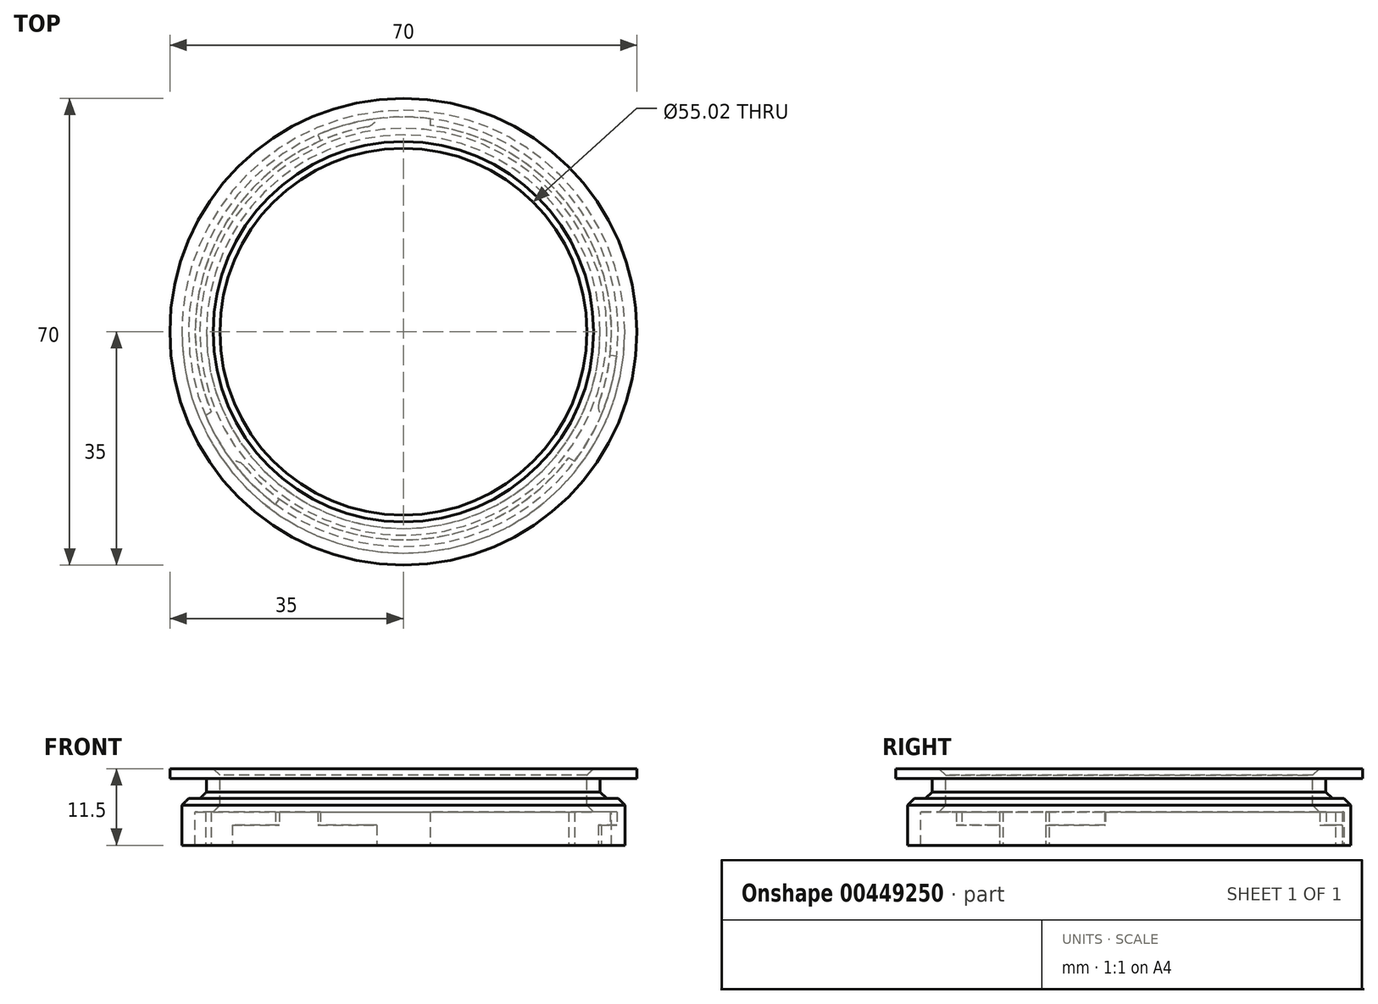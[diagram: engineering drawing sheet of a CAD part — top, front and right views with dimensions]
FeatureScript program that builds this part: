
annotation { "Feature Type Name" : "Feature", "Feature Type Description" : "" }
export const myFeature = defineFeature(function(context is Context, id is Id, definition is map)
    precondition{}
    {
        {
            var Q0;
            Q0=qCreatedBy(makeId("Front.planeOp"),FACE);
            var sketch = newSketch(context, id + "F0", { "sketchPlane" : qUnion([Q0])});
            skLineSegment(sketch, "E0.bottom", {"start": v(33.2, 3.5) * mm, "end": v(-33.2, 3.5) * mm});
            skLineSegment(sketch, "E0.top", {"start": v(33.2, -3.5) * mm, "end": v(-33.2, -3.5) * mm});
            skLineSegment(sketch, "E0.left", {"start": v(33.2, 3.5) * mm, "end": v(33.2, -3.5) * mm});
            skLineSegment(sketch, "E0.right", {"start": v(-33.2, 3.5) * mm, "end": v(-33.2, -3.5) * mm});
            skPoint(sketch, "E0.middle", {"position": v(0, 0) * mm});
            skLineSegment(sketch, "E1.bottom", {"start": v(29.5, 6.5) * mm, "end": v(-29.5, 6.5) * mm});
            skLineSegment(sketch, "E1.left", {"start": v(29.5, 6.5) * mm, "end": v(29.5, -3.5) * mm});
            skLineSegment(sketch, "E1.right", {"start": v(-29.5, 6.5) * mm, "end": v(-29.5, -3.5) * mm});
            skLineSegment(sketch, "E2.bottom", {"start": v(35, 9.5) * mm, "end": v(-35, 9.5) * mm});
            skLineSegment(sketch, "E2.top", {"start": v(35, 6.5) * mm, "end": v(-35, 6.5) * mm});
            skLineSegment(sketch, "E2.left", {"start": v(35, 9.5) * mm, "end": v(35, 6.5) * mm});
            skLineSegment(sketch, "E2.right", {"start": v(-35, 9.5) * mm, "end": v(-35, 6.5) * mm});
            skPoint(sketch, "E2.middle", {"position": v(0, 8) * mm});
            skPoint(sketch, "E2.middle.positionSnap0", {"position": v(0, 6.5) * mm});
            skPoint(sketch, "E2.centerSnap0", {"position": v(0, 6.5) * mm});
            skPoint(sketch, "E3.orphan", {"position": v(-29.5, -6.5) * mm});
            skPoint(sketch, "E1.top.start.orphan", {"position": v(29.5, -6.5) * mm});
            skPoint(sketch, "E4.orphan", {"position": v(0, -6.5) * mm});
            skLineSegment(sketch, "E5", {"start": v(31.2, -3.5) * mm, "end": v(31.2, 1.5) * mm});
            skLineSegment(sketch, "E6", {"start": v(31.2, 1.5) * mm, "end": v(27.5, 1.5) * mm});
            skLineSegment(sketch, "E7", {"start": v(27.5, 1.5) * mm, "end": v(27.5, 9.5) * mm});
            skLineSegment(sketch, "E8", {"start": v(0, 12.55) * mm, "end": v(0, -12.38) * mm});
            skLineSegment(sketch, "E9", {"start": v(-35, 8) * mm, "end": v(35, 8) * mm});
            skSolve(sketch);
        }
        {
            var Q0;
            {var subQ5=sQuery(id+"F0.wireOp",EDGE,"E0.left");Q0=makeQuery(id+"F0.imprint","IMPRINT",FACE,{"disambiguationData":[TD([[makeQuery(id+"F0.imprint","IMPRINT",EDGE,{"derivedFrom":subQ5}),-1.0]])]});}
            var Q1;
            {var subQ0=sQuery(id+"F0.wireOp",EDGE,"E1.left");var subQ1=sQuery(id+"F0.wireOp",EDGE,"E0.bottom");var subQ2=makeQuery(id+"F0.imprint","INTERSECT",VERTEX,{"derivedFrom":[subQ1,subQ0]});Q1=makeQuery(id+"F0.imprint","IMPRINT",FACE,{"disambiguationData":[TD([[makeQuery(id+"F0.imprint","IMPRINT",EDGE,{"disambiguationData":[TD([[subQ2,-1.0]])],"derivedFrom":subQ1}),1.0]])]});}
            var Q2;
            {var subQ0=sQuery(id+"F0.wireOp",EDGE,"E1.left");var subQ1=sQuery(id+"F0.wireOp",EDGE,"E0.bottom");var subQ2=makeQuery(id+"F0.imprint","INTERSECT",VERTEX,{"derivedFrom":[subQ1,subQ0]});Q2=makeQuery(id+"F0.imprint","IMPRINT",FACE,{"disambiguationData":[TD([[makeQuery(id+"F0.imprint","IMPRINT",EDGE,{"disambiguationData":[TD([[subQ2,-1.0]])],"derivedFrom":subQ1}),-1.0]])]});}
            var Q3;
            {var subQ1=sQuery(id+"F0.wireOp",EDGE,"E2.top");var subQ8=makeQuery(id+"F0.imprint","INTERSECT",VERTEX,{"derivedFrom":[sQuery(id+"F0.wireOp",EDGE,"E1.left"),subQ1]});Q3=makeQuery(id+"F0.imprint","IMPRINT",FACE,{"disambiguationData":[TD([[makeQuery(id+"F0.imprint","IMPRINT",EDGE,{"disambiguationData":[TD([[subQ8,1.0]])],"derivedFrom":subQ1}),-1.0]])]});}
            var Q4;
            Q4=sQuery(id+"F0.wireOp",EDGE,"E8");
            revolve(context, id + "F1", {"entities" : qUnion([Q0, Q1, Q2, Q3]), "axis" : qUnion([Q4]), "revolveType" : RevolveType.FULL});
        }
        {
            var Q0;
            Q0=makeQuery(id+"F1.opRevolve","SWEPT_EDGE",EDGE,{"disambiguationData":[OSD([sQuery(id+"F0.wireOp",EDGE,"E0.bottom"),sQuery(id+"F0.wireOp",EDGE,"E0.left")])]});
            var Q1;
            Q1=makeQuery(id+"F1.opRevolve","SWEPT_EDGE",EDGE,{"disambiguationData":[OSD([sQuery(id+"F0.wireOp",EDGE,"E6"),sQuery(id+"F0.wireOp",EDGE,"E7")])]});
            var Q2;
            Q2=makeQuery(id+"F1.opRevolve","SWEPT_EDGE",EDGE,{"disambiguationData":[OSD([sQuery(id+"F0.wireOp",EDGE,"E2.bottom"),sQuery(id+"F0.wireOp",EDGE,"E7")])]});
            var Q3;
            Q3=makeQuery(id+"F1.opRevolve","SWEPT_EDGE",EDGE,{"disambiguationData":[OSD([sQuery(id+"F0.wireOp",EDGE,"E0.bottom"),sQuery(id+"F0.wireOp",EDGE,"E1.left")])]});
            chamfer(context, id + "F2", {"entities" : qUnion([Q0, Q1, Q2, Q3]), "width" : 1 * mm, "tangentPropagation" : true});
        }
        {
            var Q0;
            Q0=makeQuery(id+"F1.opRevolve","SWEPT_FACE",FACE,{"disambiguationData":[OSD([sQuery(id+"F0.wireOp",EDGE,"E0.top")])]});
            var sketch = newSketch(context, id + "F3", { "sketchPlane" : qUnion([Q0])});
            skCircle(sketch, "E10", {"center": v(0, 0) * mm, "radius": 33.2 * mm});
            skCircle(sketch, "E11.0", {"center": v(0, 0) * mm, "radius": 32.2 * mm});
            skLineSegment(sketch, "E12", {"start": v(4, -31.95) * mm, "end": v(4, -30.94) * mm});
            skLineSegment(sketch, "E13.MirrorCS", {"start": v(-4, -31.95) * mm, "end": v(-4, -30.94) * mm});
            skLineSegment(sketch, "E14", {"start": v(0, 0) * mm, "end": v(-12.83, -29.53) * mm});
            skArc(sketch, "E15", {"start": v(4, -30.94) * mm, "mid": v(0, 31.2) * mm, "end": v(-4, -30.94) * mm});
            skLineSegment(sketch, "E16.1.0", {"start": v(25.67, 19.44) * mm, "end": v(24.8, 18.94) * mm});
            skLineSegment(sketch, "E16.1.1", {"start": v(29.67, 12.51) * mm, "end": v(28.8, 12) * mm});
            skLineSegment(sketch, "E16.1.2", {"start": v(0, 0) * mm, "end": v(32, 3.66) * mm});
            skLineSegment(sketch, "E16.2.0", {"start": v(-29.67, 12.51) * mm, "end": v(-28.8, 12) * mm});
            skLineSegment(sketch, "E16.2.1", {"start": v(-25.67, 19.44) * mm, "end": v(-24.8, 18.94) * mm});
            skLineSegment(sketch, "E16.2.2", {"start": v(0, 0) * mm, "end": v(-19.16, 25.88) * mm});
            skSolve(sketch);
        }
        {
            var Q0;
            {var subQ0=sQuery(id+"F3.wireOp",EDGE,"E12");Q0=makeQuery(id+"F3.imprint","IMPRINT",FACE,{"disambiguationData":[TD([[makeQuery(id+"F3.imprint","IMPRINT",EDGE,{"derivedFrom":subQ0}),1.0]])]});}
            var Q1;
            {var subQ0=sQuery(id+"F3.wireOp",EDGE,"E13.MirrorCS");Q1=makeQuery(id+"F3.imprint","IMPRINT",FACE,{"disambiguationData":[TD([[makeQuery(id+"F3.imprint","IMPRINT",EDGE,{"derivedFrom":subQ0}),1.0]])]});}
            var Q2;
            {var subQ0=sQuery(id+"F3.wireOp",EDGE,"E16.2.0");Q2=makeQuery(id+"F3.imprint","IMPRINT",FACE,{"disambiguationData":[TD([[makeQuery(id+"F3.imprint","IMPRINT",EDGE,{"derivedFrom":subQ0}),1.0]])]});}
            var Q3;
            {var subQ0=sQuery(id+"F3.wireOp",EDGE,"E16.2.1");Q3=makeQuery(id+"F3.imprint","IMPRINT",FACE,{"disambiguationData":[TD([[makeQuery(id+"F3.imprint","IMPRINT",EDGE,{"derivedFrom":subQ0}),1.0]])]});}
            var Q4;
            {var subQ0=sQuery(id+"F3.wireOp",EDGE,"E16.1.1");Q4=makeQuery(id+"F3.imprint","IMPRINT",FACE,{"disambiguationData":[TD([[makeQuery(id+"F3.imprint","IMPRINT",EDGE,{"derivedFrom":subQ0}),1.0]])]});}
            var Q5;
            {var subQ0=sQuery(id+"F3.wireOp",EDGE,"E16.1.0");Q5=makeQuery(id+"F3.imprint","IMPRINT",FACE,{"disambiguationData":[TD([[makeQuery(id+"F3.imprint","IMPRINT",EDGE,{"derivedFrom":subQ0}),1.0]])]});}
            var Q6;
            Q6=makeQuery(id+"F1.opRevolve","SWEPT_FACE",FACE,{"disambiguationData":[OSD([sQuery(id+"F0.wireOp",EDGE,"E6")])]});
            extrude(context, id + "F4", {"entities" : qUnion([Q0, Q1, Q2, Q3, Q4, Q5]), "operationType" : NewBodyOperationType.REMOVE, "endBound" : BoundingType.UP_TO_SURFACE, "oppositeDirection" : true, "endBoundEntityFace" : qUnion([Q6]), "depth" : 25 * mm});
        }
        {
            var Q0;
            {var subQ0=sQuery(id+"F3.wireOp",EDGE,"E13.MirrorCS");Q0=makeQuery(id+"F3.imprint","IMPRINT",FACE,{"disambiguationData":[TD([[makeQuery(id+"F3.imprint","IMPRINT",EDGE,{"derivedFrom":subQ0}),1.0]])]});}
            var Q1;
            {var subQ0=sQuery(id+"F3.wireOp",EDGE,"E16.2.1");Q1=makeQuery(id+"F3.imprint","IMPRINT",FACE,{"disambiguationData":[TD([[makeQuery(id+"F3.imprint","IMPRINT",EDGE,{"derivedFrom":subQ0}),1.0]])]});}
            var Q2;
            {var subQ0=sQuery(id+"F3.wireOp",EDGE,"E16.1.1");Q2=makeQuery(id+"F3.imprint","IMPRINT",FACE,{"disambiguationData":[TD([[makeQuery(id+"F3.imprint","IMPRINT",EDGE,{"derivedFrom":subQ0}),1.0]])]});}
            extrude(context, id + "F5", {"entities" : qUnion([Q0, Q1, Q2]), "operationType" : NewBodyOperationType.ADD, "oppositeDirection" : true, "depth" : 3 * mm});
        }
        {
            var Q0;
            Q0=makeQuery(id+"F5.opExtrude","SWEPT_EDGE",EDGE,{"disambiguationData":[OSD([sQuery(id+"F0.wireOp",EDGE,"E0.top"),sQuery(id+"F0.wireOp",EDGE,"E5"),sQuery(id+"F3.wireOp",EDGE,"E13.MirrorCS"),sQuery(id+"F3.wireOp",EDGE,"E15")])]});
            var Q1;
            Q1=makeQuery(id+"F5.opExtrude","SWEPT_EDGE",EDGE,{"disambiguationData":[OSD([sQuery(id+"F3.wireOp",EDGE,"E15"),sQuery(id+"F3.wireOp",EDGE,"E16.2.1")])]});
            var Q2;
            Q2=makeQuery(id+"F5.opExtrude","SWEPT_EDGE",EDGE,{"disambiguationData":[OSD([sQuery(id+"F3.wireOp",EDGE,"E15"),sQuery(id+"F3.wireOp",EDGE,"E16.1.1")])]});
            fillet(context, id + "F6", {"entities" : qUnion([Q0, Q1, Q2]), "radius" : 2 * mm, "tangentPropagation" : true, "allowEdgeOverflow" : false});
        }
    });
